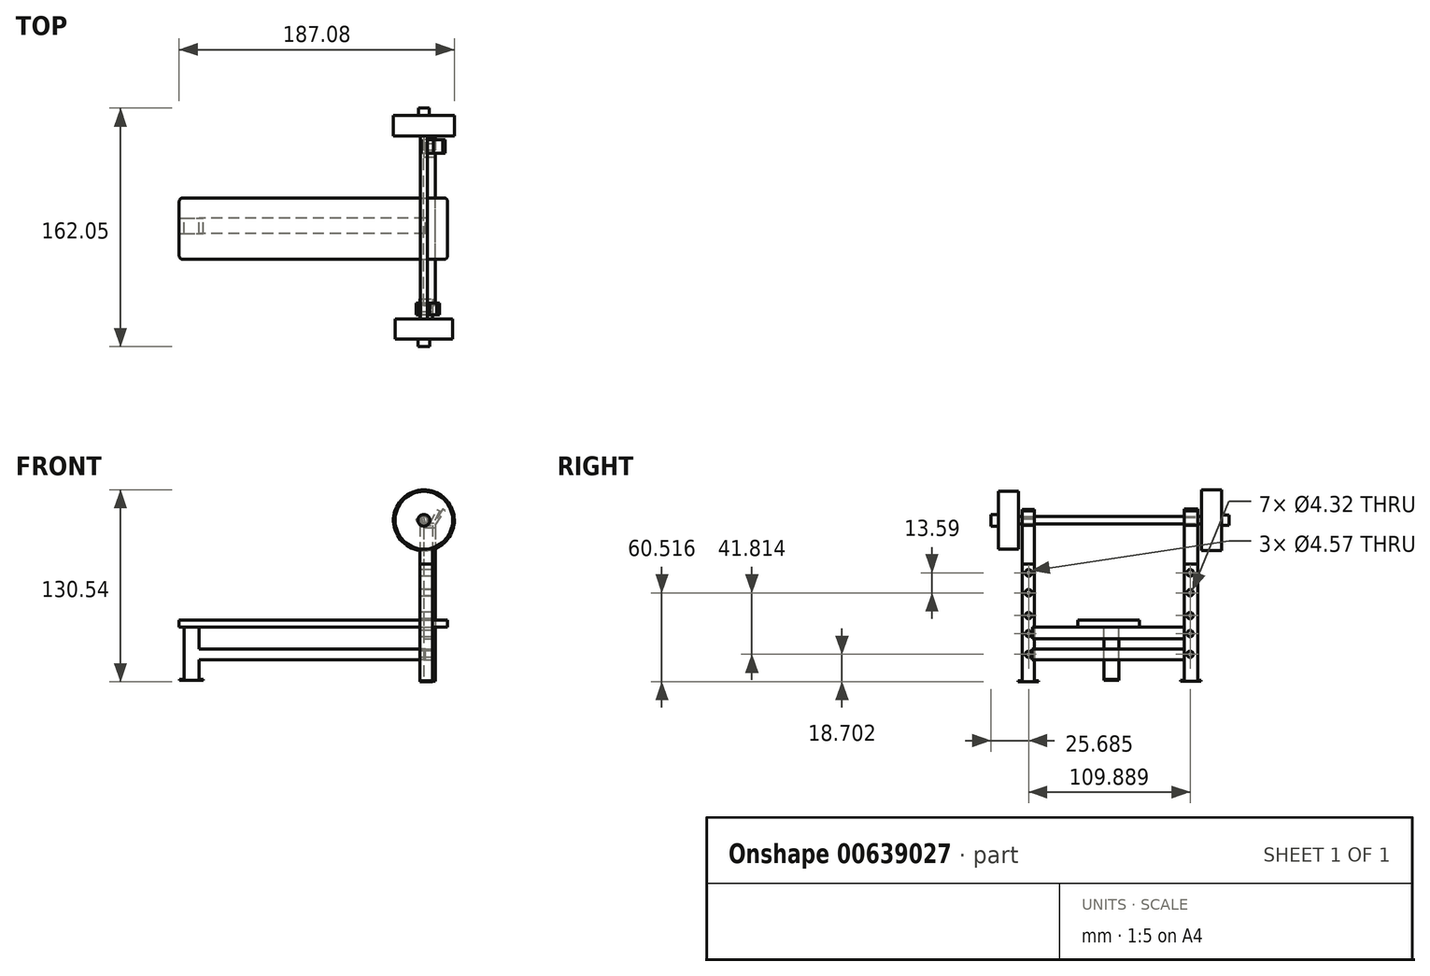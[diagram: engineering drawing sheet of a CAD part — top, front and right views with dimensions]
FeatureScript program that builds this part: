
annotation { "Feature Type Name" : "Feature", "Feature Type Description" : "" }
export const myFeature = defineFeature(function(context is Context, id is Id, definition is map)
    precondition{}
    {
        {
            var Q0;
            Q0=qCreatedBy(makeId("Top.planeOp"),FACE);
            var sketch = newSketch(context, id + "F0", { "sketchPlane" : qUnion([Q0])});
            skLineSegment(sketch, "E0.bottom", {"start": v(-59.94, -49.2) * mm, "end": v(122.61, -49.2) * mm});
            skLineSegment(sketch, "E0.top", {"start": v(-59.94, -7.42) * mm, "end": v(122.61, -7.42) * mm});
            skLineSegment(sketch, "E0.left", {"start": v(-59.94, -49.2) * mm, "end": v(-59.94, -7.42) * mm});
            skLineSegment(sketch, "E0.right", {"start": v(122.61, -49.2) * mm, "end": v(122.61, -7.42) * mm});
            skSolve(sketch);
        }
        {
            var Q0;
            Q0 = qSketchRegion(id + "F0", true);
            extrude(context, id + "F1", {"entities" : qUnion([Q0]), "depth" : 4.83 * mm, "offsetDistance" : 25.4 * mm});
        }
        {
            var Q0;
            Q0=makeQuery(id+"F1.opExtrude","CAP_FACE",FACE,{"disambiguationData":[OSD([sQuery(id+"F0.wireOp",EDGE,"E0.bottom"),sQuery(id+"F0.wireOp",EDGE,"E0.top"),sQuery(id+"F0.wireOp",EDGE,"E0.left"),sQuery(id+"F0.wireOp",EDGE,"E0.right")])],"isStart":true});
            var sketch = newSketch(context, id + "F2", { "sketchPlane" : qUnion([Q0])});
            skLineSegment(sketch, "E1.bottom", {"start": v(-56.7, 31.62) * mm, "end": v(-46.5, 31.62) * mm});
            skLineSegment(sketch, "E1.top", {"start": v(-56.7, 21.21) * mm, "end": v(-46.5, 21.21) * mm});
            skLineSegment(sketch, "E1.left", {"start": v(-56.7, 31.62) * mm, "end": v(-56.7, 21.21) * mm});
            skLineSegment(sketch, "E1.right", {"start": v(-46.5, 31.62) * mm, "end": v(-46.5, 21.21) * mm});
            skSolve(sketch);
        }
        {
            var Q0;
            Q0 = qSketchRegion(id + "F2", true);
            extrude(context, id + "F3", {"entities" : qUnion([Q0]), "operationType" : NewBodyOperationType.ADD, "depth" : 35.56 * mm, "offsetDistance" : 25.4 * mm});
        }
        {
            var Q0;
            Q0=makeQuery(id+"F3.opExtrude","CAP_FACE",FACE,{"disambiguationData":[OSD([sQuery(id+"F2.wireOp",EDGE,"E1.bottom"),sQuery(id+"F2.wireOp",EDGE,"E1.top"),sQuery(id+"F2.wireOp",EDGE,"E1.left"),sQuery(id+"F2.wireOp",EDGE,"E1.right")])],"isStart":false});
            var sketch = newSketch(context, id + "F4", { "sketchPlane" : qUnion([Q0])});
            skPoint(sketch, "E2.firstSnap0", {"position": v(-51.6, 31.62) * mm});
            skLineSegment(sketch, "E2.bottom", {"start": v(-59.86, 31.62) * mm, "end": v(-43.73, 31.62) * mm});
            skLineSegment(sketch, "E2.top", {"start": v(-59.86, 21.21) * mm, "end": v(-43.73, 21.21) * mm});
            skLineSegment(sketch, "E2.left", {"start": v(-59.86, 31.62) * mm, "end": v(-59.86, 21.21) * mm});
            skLineSegment(sketch, "E2.right", {"start": v(-43.73, 31.62) * mm, "end": v(-43.73, 21.21) * mm});
            skSolve(sketch);
        }
        {
            var Q0;
            Q0 = qSketchRegion(id + "F4", true);
            extrude(context, id + "F5", {"entities" : qUnion([Q0]), "operationType" : NewBodyOperationType.ADD, "depth" : 0.5 * mm, "offsetDistance" : 25.4 * mm});
        }
        {
            var Q0;
            Q0=makeQuery(id+"F3.opExtrude","SWEPT_FACE",FACE,{"disambiguationData":[OSD([sQuery(id+"F2.wireOp",EDGE,"E1.right")])]});
            var sketch = newSketch(context, id + "F6", { "sketchPlane" : qUnion([Q0])});
            skLineSegment(sketch, "E3.bottom", {"start": v(-31.62, -14.93) * mm, "end": v(-21.21, -14.93) * mm});
            skLineSegment(sketch, "E3.top", {"start": v(-31.62, -22.2) * mm, "end": v(-21.21, -22.2) * mm});
            skLineSegment(sketch, "E3.left", {"start": v(-31.62, -14.93) * mm, "end": v(-31.62, -22.2) * mm});
            skLineSegment(sketch, "E3.right", {"start": v(-21.21, -14.93) * mm, "end": v(-21.21, -22.2) * mm});
            skSolve(sketch);
        }
        {
            var Q0;
            Q0 = qSketchRegion(id + "F6", true);
            extrude(context, id + "F7", {"entities" : qUnion([Q0]), "operationType" : NewBodyOperationType.ADD, "depth" : 153.92 * mm, "offsetDistance" : 25.4 * mm});
        }
        {
            var Q0;
            Q0=qCreatedBy(makeId("Top.planeOp"),FACE);
            var sketch = newSketch(context, id + "F8", { "sketchPlane" : qUnion([Q0])});
            skLineSegment(sketch, "E4.bottom", {"start": v(112.29, -78.86) * mm, "end": v(103.9, -78.86) * mm});
            skLineSegment(sketch, "E4.top", {"start": v(112.29, -87.02) * mm, "end": v(103.9, -87.02) * mm});
            skLineSegment(sketch, "E4.left", {"start": v(112.29, -78.86) * mm, "end": v(112.29, -87.02) * mm});
            skLineSegment(sketch, "E4.right", {"start": v(103.9, -78.86) * mm, "end": v(103.9, -87.02) * mm});
            skSolve(sketch);
        }
        {
            var Q0;
            Q0 = qSketchRegion(id + "F8", true);
            extrude(context, id + "F9", {"entities" : qUnion([Q0]), "depth" : 42.93 * mm, "offsetDistance" : 25.4 * mm, "hasSecondDirection" : true, "secondDirectionOppositeDirection" : true, "secondDirectionDepth" : 36.32 * mm});
        }
        {
            var Q0;
            Q0=qCreatedBy(makeId("Top.planeOp"),FACE);
            var sketch = newSketch(context, id + "F10", { "sketchPlane" : qUnion([Q0])});
            skLineSegment(sketch, "E5.bottom", {"start": v(114.2, 32.2) * mm, "end": v(106.23, 32.2) * mm});
            skLineSegment(sketch, "E5.top", {"start": v(114.2, 23.11) * mm, "end": v(106.23, 23.11) * mm});
            skLineSegment(sketch, "E5.left", {"start": v(114.2, 32.2) * mm, "end": v(114.2, 23.11) * mm});
            skLineSegment(sketch, "E5.right", {"start": v(106.23, 32.2) * mm, "end": v(106.23, 23.11) * mm});
            skSolve(sketch);
        }
        {
            var Q0;
            Q0 = qSketchRegion(id + "F10", true);
            extrude(context, id + "F11", {"entities" : qUnion([Q0]), "depth" : 42.93 * mm, "offsetDistance" : 25.4 * mm, "hasSecondDirection" : true, "secondDirectionOppositeDirection" : true, "secondDirectionDepth" : 36.07 * mm});
        }
        {
            var Q0;
            Q0=makeQuery(id+"F11.opExtrude","SWEPT_FACE",FACE,{"disambiguationData":[OSD([sQuery(id+"F10.wireOp",EDGE,"E5.top")])]});
            var sketch = newSketch(context, id + "F12", { "sketchPlane" : qUnion([Q0])});
            skLineSegment(sketch, "E6.bottom", {"start": v(106.23, -14.93) * mm, "end": v(114.2, -14.93) * mm});
            skLineSegment(sketch, "E6.top", {"start": v(106.23, -22.2) * mm, "end": v(114.2, -22.2) * mm});
            skLineSegment(sketch, "E6.left", {"start": v(106.23, -14.93) * mm, "end": v(106.23, -22.2) * mm});
            skLineSegment(sketch, "E6.right", {"start": v(114.2, -14.93) * mm, "end": v(114.2, -22.2) * mm});
            skSolve(sketch);
        }
        {
            var Q0;
            Q0=makeQuery(id+"F12.imprint","IMPRINT",FACE,{"disambiguationData":[TD([[makeQuery(id+"F12.imprint","IMPRINT",EDGE,{"derivedFrom":sQuery(id+"F12.wireOp",EDGE,"E6.bottom")}),-1.0]])]});
            extrude(context, id + "F13", {"entities" : qUnion([Q0]), "depth" : 103.63 * mm, "offsetDistance" : 25.4 * mm});
        }
        {
            var Q0;
            Q0=makeQuery(id+"F9.opExtrude","CAP_FACE",FACE,{"disambiguationData":[OSD([sQuery(id+"F8.wireOp",EDGE,"E4.bottom"),sQuery(id+"F8.wireOp",EDGE,"E4.top"),sQuery(id+"F8.wireOp",EDGE,"E4.left"),sQuery(id+"F8.wireOp",EDGE,"E4.right")])],"isStart":false});
            var sketch = newSketch(context, id + "F14", { "sketchPlane" : qUnion([Q0])});
            skLineSegment(sketch, "E7.bottom", {"start": v(103.9, -78.86) * mm, "end": v(112.29, -78.86) * mm});
            skLineSegment(sketch, "E7.top", {"start": v(103.9, -87.02) * mm, "end": v(112.29, -87.02) * mm});
            skLineSegment(sketch, "E7.left", {"start": v(103.9, -78.86) * mm, "end": v(103.9, -87.02) * mm});
            skLineSegment(sketch, "E7.right", {"start": v(112.29, -78.86) * mm, "end": v(112.29, -87.02) * mm});
            skSolve(sketch);
        }
        {
            var Q0;
            Q0 = qSketchRegion(id + "F14", true);
            extrude(context, id + "F15", {"entities" : qUnion([Q0]), "depth" : 26.42 * mm, "offsetDistance" : 25.4 * mm});
        }
        {
            var Q0;
            Q0=makeQuery(id+"F11.opExtrude","CAP_FACE",FACE,{"disambiguationData":[OSD([sQuery(id+"F10.wireOp",EDGE,"E5.bottom"),sQuery(id+"F10.wireOp",EDGE,"E5.top"),sQuery(id+"F10.wireOp",EDGE,"E5.left"),sQuery(id+"F10.wireOp",EDGE,"E5.right")])],"isStart":false});
            var sketch = newSketch(context, id + "F16", { "sketchPlane" : qUnion([Q0])});
            skLineSegment(sketch, "E8.bottom", {"start": v(106.23, 23.11) * mm, "end": v(114.2, 23.11) * mm});
            skLineSegment(sketch, "E8.top", {"start": v(106.23, 32.2) * mm, "end": v(114.2, 32.2) * mm});
            skLineSegment(sketch, "E8.left", {"start": v(106.23, 23.11) * mm, "end": v(106.23, 32.2) * mm});
            skLineSegment(sketch, "E8.right", {"start": v(114.2, 23.11) * mm, "end": v(114.2, 32.2) * mm});
            skSolve(sketch);
        }
        {
            var Q0;
            Q0 = qSketchRegion(id + "F16", true);
            extrude(context, id + "F17", {"entities" : qUnion([Q0]), "depth" : 26.42 * mm, "offsetDistance" : 25.4 * mm});
        }
        {
            var Q0;
            Q0=makeQuery(id+"F11.opExtrude","SWEPT_FACE",FACE,{"disambiguationData":[OSD([sQuery(id+"F10.wireOp",EDGE,"E5.top")])]});
            var sketch = newSketch(context, id + "F18", { "sketchPlane" : qUnion([Q0])});
            skLineSegment(sketch, "E9.bottom", {"start": v(106.23, 0.03) * mm, "end": v(114.2, 0.03) * mm});
            skLineSegment(sketch, "E9.top", {"start": v(106.23, -7.95) * mm, "end": v(114.2, -7.95) * mm});
            skLineSegment(sketch, "E9.left", {"start": v(106.23, 0.03) * mm, "end": v(106.23, -7.95) * mm});
            skLineSegment(sketch, "E9.right", {"start": v(114.2, 0.03) * mm, "end": v(114.2, -7.95) * mm});
            skSolve(sketch);
        }
        {
            var Q0;
            Q0=makeQuery(id+"F18.imprint","IMPRINT",FACE,{"disambiguationData":[TD([[makeQuery(id+"F18.imprint","IMPRINT",EDGE,{"derivedFrom":sQuery(id+"F18.wireOp",EDGE,"E9.bottom")}),-1.0]])]});
            extrude(context, id + "F19", {"entities" : qUnion([Q0]), "depth" : 103.3 * mm, "offsetDistance" : 25.4 * mm});
        }
        {
            var Q0;
            Q0=makeQuery(id+"F15.opExtrude","SWEPT_FACE",FACE,{"disambiguationData":[OSD([sQuery(id+"F14.wireOp",EDGE,"E7.top")])]});
            var sketch = newSketch(context, id + "F20", { "sketchPlane" : qUnion([Q0])});
            skLineSegment(sketch, "E10", {"start": v(103.9, 67.64) * mm, "end": v(103.9, 69.34) * mm});
            skLineSegment(sketch, "E11", {"start": v(103.9, 69.34) * mm, "end": v(101.28, 73.42) * mm});
            skLineSegment(sketch, "E12", {"start": v(101.28, 73.42) * mm, "end": v(102.32, 74.1) * mm});
            skLineSegment(sketch, "E13", {"start": v(102.32, 74.1) * mm, "end": v(104.75, 70.3) * mm});
            skLineSegment(sketch, "E14", {"start": v(104.75, 70.3) * mm, "end": v(110.53, 70.3) * mm});
            skLineSegment(sketch, "E15", {"start": v(110.53, 70.3) * mm, "end": v(115.2, 80.07) * mm});
            skLineSegment(sketch, "E16", {"start": v(115.2, 80.07) * mm, "end": v(117, 79.21) * mm});
            skLineSegment(sketch, "E17", {"start": v(117, 79.21) * mm, "end": v(112.29, 69.34) * mm});
            skLineSegment(sketch, "E18", {"start": v(112.29, 69.34) * mm, "end": v(112.29, 67.64) * mm});
            skLineSegment(sketch, "E19", {"start": v(112.29, 67.64) * mm, "end": v(103.9, 67.64) * mm});
            skSolve(sketch);
        }
        {
            var Q0;
            Q0 = qSketchRegion(id + "F20", true);
            extrude(context, id + "F21", {"entities" : qUnion([Q0]), "operationType" : NewBodyOperationType.ADD, "oppositeDirection" : true, "depth" : 8.08 * mm, "offsetDistance" : 25.4 * mm});
        }
        {
            var Q0;
            Q0=makeQuery(id+"F17.opExtrude","SWEPT_FACE",FACE,{"disambiguationData":[OSD([sQuery(id+"F16.wireOp",EDGE,"E8.top")])]});
            var sketch = newSketch(context, id + "F22", { "sketchPlane" : qUnion([Q0])});
            skLineSegment(sketch, "E20", {"start": v(-114.2, 67.37) * mm, "end": v(-114.2, 69.34) * mm});
            skLineSegment(sketch, "E21", {"start": v(-114.2, 69.34) * mm, "end": v(-120.93, 79.26) * mm});
            skLineSegment(sketch, "E22", {"start": v(-120.93, 79.26) * mm, "end": v(-119.4, 80.3) * mm});
            skLineSegment(sketch, "E23", {"start": v(-119.4, 80.3) * mm, "end": v(-112.91, 70.73) * mm});
            skLineSegment(sketch, "E24", {"start": v(-112.91, 70.73) * mm, "end": v(-107.5, 70.73) * mm});
            skLineSegment(sketch, "E25", {"start": v(-107.5, 70.73) * mm, "end": v(-106.23, 75.2) * mm});
            skLineSegment(sketch, "E26", {"start": v(-106.23, 75.2) * mm, "end": v(-104.68, 74.76) * mm});
            skLineSegment(sketch, "E27", {"start": v(-104.68, 74.76) * mm, "end": v(-106.23, 69.34) * mm});
            skLineSegment(sketch, "E28", {"start": v(-106.23, 69.34) * mm, "end": v(-106.23, 67.37) * mm});
            skLineSegment(sketch, "E29", {"start": v(-106.23, 67.37) * mm, "end": v(-114.2, 67.37) * mm});
            skSolve(sketch);
        }
        {
            var Q0;
            Q0 = qSketchRegion(id + "F22", true);
            extrude(context, id + "F23", {"entities" : qUnion([Q0]), "operationType" : NewBodyOperationType.ADD, "oppositeDirection" : true, "depth" : 9.14 * mm, "offsetDistance" : 25.4 * mm});
        }
        {
            var Q0;
            Q0=makeQuery(id+"F1.opExtrude","SWEPT_EDGE",EDGE,{"disambiguationData":[OSD([sQuery(id+"F0.wireOp",EDGE,"E0.bottom"),sQuery(id+"F0.wireOp",EDGE,"E0.left")])]});
            var Q1;
            Q1=makeQuery(id+"F1.opExtrude","SWEPT_EDGE",EDGE,{"disambiguationData":[OSD([sQuery(id+"F0.wireOp",EDGE,"E0.top"),sQuery(id+"F0.wireOp",EDGE,"E0.left")])]});
            var Q2;
            Q2=makeQuery(id+"F1.opExtrude","SWEPT_EDGE",EDGE,{"disambiguationData":[OSD([sQuery(id+"F0.wireOp",EDGE,"E0.top"),sQuery(id+"F0.wireOp",EDGE,"E0.right")])]});
            var Q3;
            Q3=makeQuery(id+"F1.opExtrude","SWEPT_EDGE",EDGE,{"disambiguationData":[OSD([sQuery(id+"F0.wireOp",EDGE,"E0.bottom"),sQuery(id+"F0.wireOp",EDGE,"E0.right")])]});
            fillet(context, id + "F24", {"entities" : qUnion([Q0, Q1, Q2, Q3]), "radius" : 2.54 * mm, "tangentPropagation" : true, "allowEdgeOverflow" : false});
        }
        {
            var Q0;
            Q0=qCreatedBy(makeId("Front.planeOp"),FACE);
            var sketch = newSketch(context, id + "F25", { "sketchPlane" : qUnion([Q0])});
            skCircle(sketch, "E30", {"center": v(106.44, 72.76) * mm, "radius": 2.47 * mm});
            skSolve(sketch);
        }
        {
            var Q0;
            Q0 = qSketchRegion(id + "F25", true);
            extrude(context, id + "F26", {"entities" : qUnion([Q0]), "depth" : 103.38 * mm, "offsetDistance" : 25.4 * mm, "hasSecondDirection" : true, "secondDirectionOppositeDirection" : true, "secondDirectionDepth" : 48.5 * mm});
        }
        {
            var Q0;
            Q0=makeQuery(id+"F26.opExtrude","CAP_FACE",FACE,{"disambiguationData":[OSD([sQuery(id+"F25.wireOp",EDGE,"E30")])],"isStart":false});
            var sketch = newSketch(context, id + "F27", { "sketchPlane" : qUnion([Q0])});
            skCircle(sketch, "E31", {"center": v(106.44, 72.76) * mm, "radius": 19.62 * mm});
            skSolve(sketch);
        }
        {
            var Q0;
            Q0 = qSketchRegion(id + "F27", true);
            extrude(context, id + "F28", {"entities" : qUnion([Q0]), "operationType" : NewBodyOperationType.ADD, "oppositeDirection" : true, "depth" : 13.72 * mm, "offsetDistance" : 25.4 * mm});
        }
        {
            var Q0;
            Q0=makeQuery(id+"F26.opExtrude","CAP_FACE",FACE,{"disambiguationData":[OSD([sQuery(id+"F25.wireOp",EDGE,"E30")])],"isStart":true});
            var sketch = newSketch(context, id + "F29", { "sketchPlane" : qUnion([Q0])});
            skCircle(sketch, "E32", {"center": v(-106.44, 72.76) * mm, "radius": 20.7 * mm});
            skSolve(sketch);
        }
        {
            var Q0;
            Q0 = qSketchRegion(id + "F29", true);
            extrude(context, id + "F30", {"entities" : qUnion([Q0]), "operationType" : NewBodyOperationType.ADD, "oppositeDirection" : true, "depth" : 13.72 * mm, "offsetDistance" : 25.4 * mm});
        }
        {
            var Q0;
            Q0=makeQuery(id+"F30.boolean.opBoolean","MERGE",FACE,{"derivedFrom":[makeQuery(id+"F26.opExtrude","CAP_FACE",FACE,{"disambiguationData":[OSD([sQuery(id+"F25.wireOp",EDGE,"E30")])],"isStart":true}),makeQuery(id+"F30.opExtrude","CAP_FACE",FACE,{"disambiguationData":[OSD([sQuery(id+"F29.wireOp",EDGE,"E32")])],"isStart":true})]});
            var sketch = newSketch(context, id + "F31", { "sketchPlane" : qUnion([Q0])});
            skCircle(sketch, "E33", {"center": v(-106.44, 72.76) * mm, "radius": 3.58 * mm});
            skSolve(sketch);
        }
        {
            var Q0;
            Q0 = qSketchRegion(id + "F31", true);
            extrude(context, id + "F32", {"entities" : qUnion([Q0]), "operationType" : NewBodyOperationType.ADD, "depth" : 5.08 * mm, "offsetDistance" : 25.4 * mm});
        }
        {
            var Q0;
            Q0=makeQuery(id+"F28.boolean.opBoolean","MERGE",FACE,{"derivedFrom":[makeQuery(id+"F26.opExtrude","CAP_FACE",FACE,{"disambiguationData":[OSD([sQuery(id+"F25.wireOp",EDGE,"E30")])],"isStart":false}),makeQuery(id+"F28.opExtrude","CAP_FACE",FACE,{"disambiguationData":[OSD([sQuery(id+"F27.wireOp",EDGE,"E31")])],"isStart":true})]});
            var sketch = newSketch(context, id + "F33", { "sketchPlane" : qUnion([Q0])});
            skCircle(sketch, "E34", {"center": v(106.44, 72.76) * mm, "radius": 4 * mm});
            skSolve(sketch);
        }
        {
            var Q0;
            Q0 = qSketchRegion(id + "F33", true);
            extrude(context, id + "F34", {"entities" : qUnion([Q0]), "operationType" : NewBodyOperationType.ADD, "depth" : 5.08 * mm, "offsetDistance" : 25.4 * mm});
        }
        {
            var Q0;
            Q0=makeQuery(id+"F9.opExtrude","SWEPT_FACE",FACE,{"disambiguationData":[OSD([sQuery(id+"F8.wireOp",EDGE,"E4.right")])]});
            var sketch = newSketch(context, id + "F35", { "sketchPlane" : qUnion([Q0])});
            skCircle(sketch, "E35", {"center": v(82.77, 37.03) * mm, "radius": 2.29 * mm});
            skSolve(sketch);
        }
        {
            var Q0;
            Q0 = qSketchRegion(id + "F35", true);
            extrude(context, id + "F36", {"entities" : qUnion([Q0]), "operationType" : NewBodyOperationType.REMOVE, "oppositeDirection" : true, "depth" : 25.4 * mm, "offsetDistance" : 25.4 * mm});
        }
        {
            var Q0;
            Q0=makeQuery(id+"F9.opExtrude","SWEPT_FACE",FACE,{"disambiguationData":[OSD([sQuery(id+"F8.wireOp",EDGE,"E4.right")])]});
            var sketch = newSketch(context, id + "F37", { "sketchPlane" : qUnion([Q0])});
            skCircle(sketch, "E36", {"center": v(82.77, 23.44) * mm, "radius": 2.29 * mm});
            skSolve(sketch);
        }
        {
            var Q0;
            Q0 = qSketchRegion(id + "F37", true);
            extrude(context, id + "F38", {"entities" : qUnion([Q0]), "operationType" : NewBodyOperationType.REMOVE, "oppositeDirection" : true, "depth" : 25.4 * mm, "offsetDistance" : 25.4 * mm});
        }
        {
            var Q0;
            Q0=makeQuery(id+"F37.imprint","IMPRINT",FACE,{"disambiguationData":[TD([[makeQuery(id+"F37.imprint","IMPRINT",EDGE,{"derivedFrom":sQuery(id+"F37.wireOp",EDGE,"E36")}),-1.0]])]});
            var sketch = newSketch(context, id + "F39", { "sketchPlane" : qUnion([Q0])});
            skCircle(sketch, "E37", {"center": v(82.77, 7.95) * mm, "radius": 2.16 * mm});
            skSolve(sketch);
        }
        {
            var Q0;
            Q0 = qSketchRegion(id + "F39", true);
            extrude(context, id + "F40", {"entities" : qUnion([Q0]), "operationType" : NewBodyOperationType.REMOVE, "oppositeDirection" : true, "depth" : 25.4 * mm, "offsetDistance" : 25.4 * mm});
        }
        {
            var Q0;
            Q0=makeQuery(id+"F35.imprint","IMPRINT",FACE,{"disambiguationData":[TD([[makeQuery(id+"F35.imprint","IMPRINT",EDGE,{"derivedFrom":sQuery(id+"F35.wireOp",EDGE,"E35")}),-1.0]])]});
            var sketch = newSketch(context, id + "F41", { "sketchPlane" : qUnion([Q0])});
            skCircle(sketch, "E38", {"center": v(82.77, -4.32) * mm, "radius": 2.16 * mm});
            skSolve(sketch);
        }
        {
            var Q0;
            Q0 = qSketchRegion(id + "F41", true);
            extrude(context, id + "F42", {"entities" : qUnion([Q0]), "operationType" : NewBodyOperationType.REMOVE, "oppositeDirection" : true, "depth" : 25.4 * mm, "offsetDistance" : 25.4 * mm});
        }
        {
            var Q0;
            Q0=makeQuery(id+"F35.imprint","IMPRINT",FACE,{"disambiguationData":[TD([[makeQuery(id+"F35.imprint","IMPRINT",EDGE,{"derivedFrom":sQuery(id+"F35.wireOp",EDGE,"E35")}),-1.0]])]});
            var sketch = newSketch(context, id + "F43", { "sketchPlane" : qUnion([Q0])});
            skCircle(sketch, "E39", {"center": v(82.77, -18.38) * mm, "radius": 2.16 * mm});
            skSolve(sketch);
        }
        {
            var Q0;
            Q0 = qSketchRegion(id + "F43", true);
            extrude(context, id + "F44", {"entities" : qUnion([Q0]), "operationType" : NewBodyOperationType.REMOVE, "oppositeDirection" : true, "depth" : 25.4 * mm, "offsetDistance" : 25.4 * mm});
        }
        {
            var Q0;
            Q0=makeQuery(id+"F11.opExtrude","SWEPT_FACE",FACE,{"disambiguationData":[OSD([sQuery(id+"F10.wireOp",EDGE,"E5.right")])]});
            var sketch = newSketch(context, id + "F45", { "sketchPlane" : qUnion([Q0])});
            skCircle(sketch, "E40", {"center": v(-27.11, 37.03) * mm, "radius": 2.29 * mm});
            skSolve(sketch);
        }
        {
            var Q0;
            Q0 = qSketchRegion(id + "F45", true);
            extrude(context, id + "F46", {"entities" : qUnion([Q0]), "operationType" : NewBodyOperationType.REMOVE, "oppositeDirection" : true, "depth" : 25.4 * mm, "offsetDistance" : 25.4 * mm});
        }
        {
            var Q0;
            Q0=makeQuery(id+"F45.imprint","IMPRINT",FACE,{"disambiguationData":[TD([[makeQuery(id+"F45.imprint","IMPRINT",EDGE,{"derivedFrom":sQuery(id+"F45.wireOp",EDGE,"E40")}),-1.0]])]});
            var sketch = newSketch(context, id + "F47", { "sketchPlane" : qUnion([Q0])});
            skCircle(sketch, "E41", {"center": v(-27.11, 23.44) * mm, "radius": 2.16 * mm});
            skSolve(sketch);
        }
        {
            var Q0;
            Q0 = qSketchRegion(id + "F47", true);
            extrude(context, id + "F48", {"entities" : qUnion([Q0]), "operationType" : NewBodyOperationType.REMOVE, "oppositeDirection" : true, "depth" : 25.4 * mm, "offsetDistance" : 25.4 * mm});
        }
        {
            var Q0;
            Q0=makeQuery(id+"F45.imprint","IMPRINT",FACE,{"disambiguationData":[TD([[makeQuery(id+"F45.imprint","IMPRINT",EDGE,{"derivedFrom":sQuery(id+"F45.wireOp",EDGE,"E40")}),-1.0]])]});
            var sketch = newSketch(context, id + "F49", { "sketchPlane" : qUnion([Q0])});
            skCircle(sketch, "E42", {"center": v(-27.11, 7.95) * mm, "radius": 2.16 * mm});
            skSolve(sketch);
        }
        {
            var Q0;
            Q0 = qSketchRegion(id + "F49", true);
            extrude(context, id + "F50", {"entities" : qUnion([Q0]), "operationType" : NewBodyOperationType.REMOVE, "oppositeDirection" : true, "depth" : 25.4 * mm, "offsetDistance" : 25.4 * mm});
        }
        {
            var Q0;
            Q0=makeQuery(id+"F45.imprint","IMPRINT",FACE,{"disambiguationData":[TD([[makeQuery(id+"F45.imprint","IMPRINT",EDGE,{"derivedFrom":sQuery(id+"F45.wireOp",EDGE,"E40")}),-1.0]])]});
            var sketch = newSketch(context, id + "F51", { "sketchPlane" : qUnion([Q0])});
            skCircle(sketch, "E43", {"center": v(-27.11, -4.32) * mm, "radius": 2.16 * mm});
            skSolve(sketch);
        }
        {
            var Q0;
            Q0 = qSketchRegion(id + "F51", true);
            extrude(context, id + "F52", {"entities" : qUnion([Q0]), "operationType" : NewBodyOperationType.REMOVE, "oppositeDirection" : true, "depth" : 25.4 * mm, "offsetDistance" : 25.4 * mm});
        }
        {
            var Q0;
            Q0=makeQuery(id+"F45.imprint","IMPRINT",FACE,{"disambiguationData":[TD([[makeQuery(id+"F45.imprint","IMPRINT",EDGE,{"derivedFrom":sQuery(id+"F45.wireOp",EDGE,"E40")}),-1.0]])]});
            var sketch = newSketch(context, id + "F53", { "sketchPlane" : qUnion([Q0])});
            skCircle(sketch, "E44", {"center": v(-27.11, -18.38) * mm, "radius": 2.16 * mm});
            skSolve(sketch);
        }
        {
            var Q0;
            Q0 = qSketchRegion(id + "F53", true);
            extrude(context, id + "F54", {"entities" : qUnion([Q0]), "operationType" : NewBodyOperationType.REMOVE, "oppositeDirection" : true, "depth" : 25.4 * mm, "offsetDistance" : 25.4 * mm});
        }
        {
            var Q0;
            Q0=makeQuery(id+"F9.opExtrude","CAP_FACE",FACE,{"disambiguationData":[OSD([sQuery(id+"F8.wireOp",EDGE,"E4.bottom"),sQuery(id+"F8.wireOp",EDGE,"E4.top"),sQuery(id+"F8.wireOp",EDGE,"E4.left"),sQuery(id+"F8.wireOp",EDGE,"E4.right")])],"isStart":true});
            var sketch = newSketch(context, id + "F55", { "sketchPlane" : qUnion([Q0])});
            skLineSegment(sketch, "E45.bottom", {"start": v(103.9, 76.07) * mm, "end": v(112.29, 76.07) * mm});
            skLineSegment(sketch, "E45.top", {"start": v(103.9, 90.03) * mm, "end": v(112.29, 90.03) * mm});
            skLineSegment(sketch, "E45.left", {"start": v(103.9, 76.07) * mm, "end": v(103.9, 90.03) * mm});
            skLineSegment(sketch, "E45.right", {"start": v(112.29, 76.07) * mm, "end": v(112.29, 90.03) * mm});
            skSolve(sketch);
        }
        {
            var Q0;
            Q0 = qSketchRegion(id + "F55", true);
            extrude(context, id + "F56", {"entities" : qUnion([Q0]), "operationType" : NewBodyOperationType.ADD, "depth" : 0.76 * mm, "offsetDistance" : 25.4 * mm});
        }
        {
            var Q0;
            Q0=makeQuery(id+"F11.opExtrude","CAP_FACE",FACE,{"disambiguationData":[OSD([sQuery(id+"F10.wireOp",EDGE,"E5.bottom"),sQuery(id+"F10.wireOp",EDGE,"E5.top"),sQuery(id+"F10.wireOp",EDGE,"E5.left"),sQuery(id+"F10.wireOp",EDGE,"E5.right")])],"isStart":true});
            var sketch = newSketch(context, id + "F57", { "sketchPlane" : qUnion([Q0])});
            skLineSegment(sketch, "E46.bottom", {"start": v(106.23, -34.5) * mm, "end": v(114.2, -34.5) * mm});
            skLineSegment(sketch, "E46.top", {"start": v(106.23, -20.53) * mm, "end": v(114.2, -20.53) * mm});
            skLineSegment(sketch, "E46.left", {"start": v(106.23, -34.5) * mm, "end": v(106.23, -20.53) * mm});
            skLineSegment(sketch, "E46.right", {"start": v(114.2, -34.5) * mm, "end": v(114.2, -20.53) * mm});
            skSolve(sketch);
        }
        {
            var Q0;
            Q0 = qSketchRegion(id + "F57", true);
            extrude(context, id + "F58", {"entities" : qUnion([Q0]), "operationType" : NewBodyOperationType.ADD, "depth" : 0.76 * mm, "offsetDistance" : 25.4 * mm});
        }
    });
